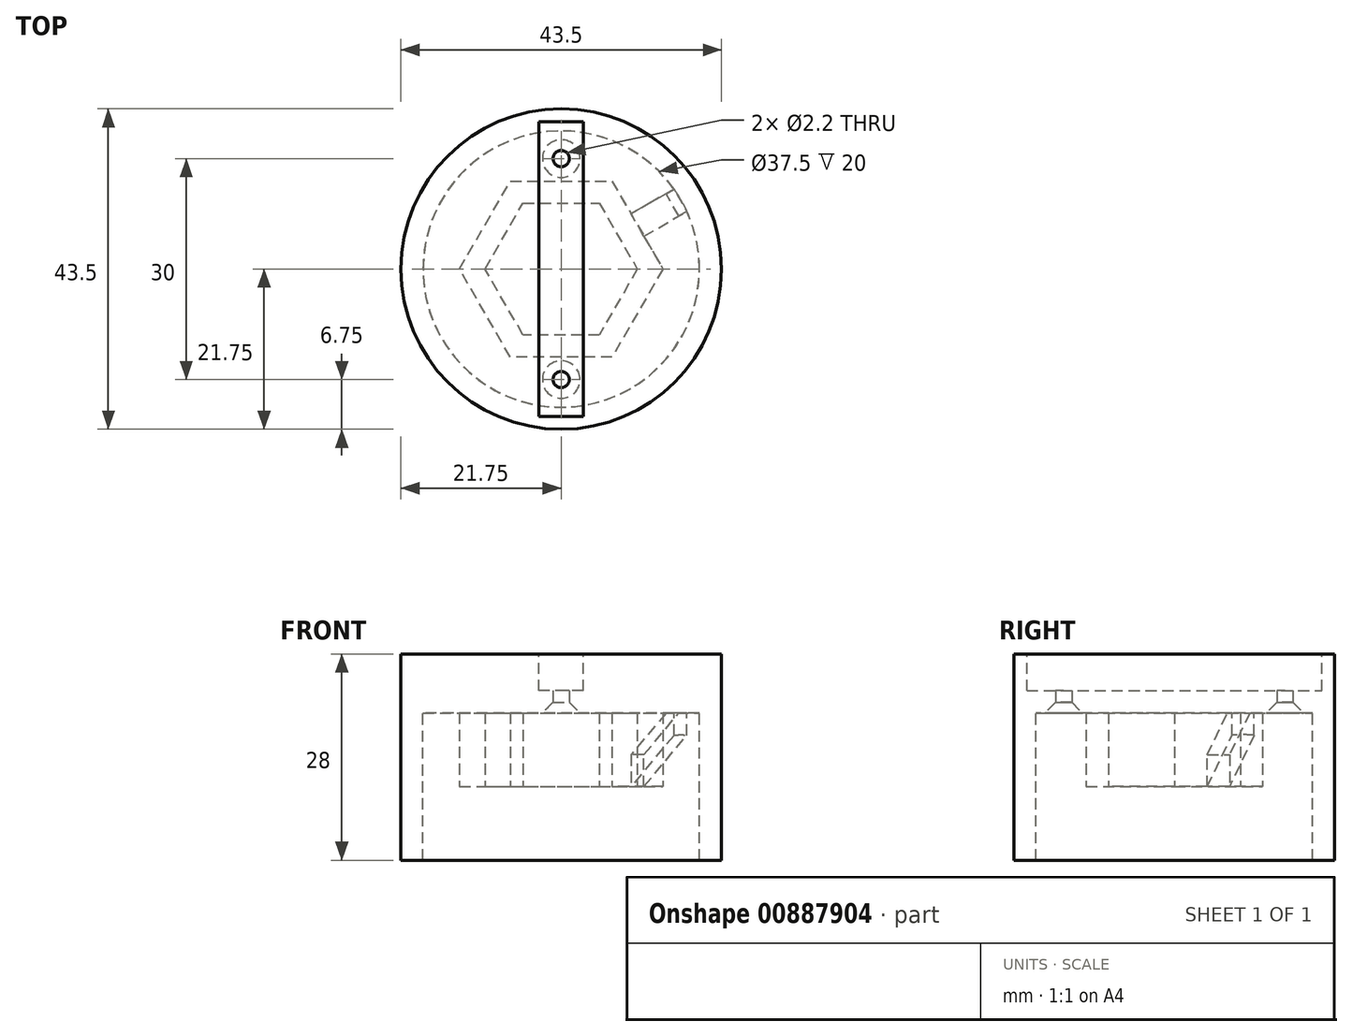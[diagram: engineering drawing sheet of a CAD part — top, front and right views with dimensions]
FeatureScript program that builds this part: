
annotation { "Feature Type Name" : "Feature", "Feature Type Description" : "" }
export const myFeature = defineFeature(function(context is Context, id is Id, definition is map)
    precondition{}
    {
        {
            var Q0;
            Q0=qCreatedBy(makeId("Top.planeOp"),FACE);
            var sketch = newSketch(context, id + "F0", { "sketchPlane" : qUnion([Q0])});
            skCircle(sketch, "E0.cCircle", {"center": v(0, 0) * mm, "radius": 8.95 * mm, "construction": true});
            skLineSegment(sketch, "E0.0", {"start": v(-5.17, 8.95) * mm, "end": v(5.17, 8.95) * mm});
            skLineSegment(sketch, "E0.1", {"start": v(5.17, 8.95) * mm, "end": v(10.33, 0) * mm});
            skLineSegment(sketch, "E0.2", {"start": v(10.33, 0) * mm, "end": v(5.17, -8.95) * mm});
            skLineSegment(sketch, "E0.3", {"start": v(5.17, -8.95) * mm, "end": v(-5.17, -8.95) * mm});
            skLineSegment(sketch, "E0.4", {"start": v(-5.17, -8.95) * mm, "end": v(-10.33, 0) * mm});
            skLineSegment(sketch, "E0.5", {"start": v(-10.33, 0) * mm, "end": v(-5.17, 8.95) * mm});
            skPoint(sketch, "E0.0.midPoint", {"position": v(0, 8.95) * mm});
            skLineSegment(sketch, "E1.0", {"start": v(-6.9, 11.95) * mm, "end": v(6.9, 11.95) * mm});
            skLineSegment(sketch, "E1.1", {"start": v(13.8, 0) * mm, "end": v(6.9, -11.95) * mm});
            skLineSegment(sketch, "E1.2", {"start": v(6.9, -11.95) * mm, "end": v(-6.9, -11.95) * mm});
            skLineSegment(sketch, "E1.3", {"start": v(6.9, 11.95) * mm, "end": v(13.8, 0) * mm});
            skLineSegment(sketch, "E1.4", {"start": v(-6.9, -11.95) * mm, "end": v(-13.8, 0) * mm});
            skLineSegment(sketch, "E1.5", {"start": v(-13.8, 0) * mm, "end": v(-6.9, 11.95) * mm});
            skSolve(sketch);
        }
        {
            var Q0;
            Q0=makeQuery(id+"F0.imprint","IMPRINT",FACE,{"disambiguationData":[TD([[makeQuery(id+"F0.imprint","IMPRINT",EDGE,{"derivedFrom":sQuery(id+"F0.wireOp",EDGE,"E0.0")}),1.0]])]});
            extrude(context, id + "F1", {"entities" : qUnion([Q0]), "depth" : 10 * mm, "offsetDistance" : 25 * mm});
        }
        {
            var Q0;
            Q0=makeQuery(id+"F1.opExtrude","CAP_FACE",FACE,{"disambiguationData":[OSD([sQuery(id+"F0.wireOp",EDGE,"E0.0"),sQuery(id+"F0.wireOp",EDGE,"E0.1"),sQuery(id+"F0.wireOp",EDGE,"E0.2"),sQuery(id+"F0.wireOp",EDGE,"E0.3"),sQuery(id+"F0.wireOp",EDGE,"E0.4"),sQuery(id+"F0.wireOp",EDGE,"E0.5"),sQuery(id+"F0.wireOp",EDGE,"E1.0"),sQuery(id+"F0.wireOp",EDGE,"E1.1"),sQuery(id+"F0.wireOp",EDGE,"E1.2"),sQuery(id+"F0.wireOp",EDGE,"E1.3"),sQuery(id+"F0.wireOp",EDGE,"E1.4"),sQuery(id+"F0.wireOp",EDGE,"E1.5")])],"isStart":false});
            var sketch = newSketch(context, id + "F2", { "sketchPlane" : qUnion([Q0])});
            skCircle(sketch, "E2", {"center": v(0, 0) * mm, "radius": 21.75 * mm});
            skCircle(sketch, "E3.0", {"center": v(0, 0) * mm, "radius": 18.75 * mm});
            skSolve(sketch);
        }
        {
            var Q0;
            Q0=makeQuery(id+"F2.imprint","IMPRINT",FACE,{"disambiguationData":[TD([[makeQuery(id+"F2.imprint","IMPRINT",EDGE,{"derivedFrom":sQuery(id+"F2.wireOp",EDGE,"E2")}),1.0]])]});
            extrude(context, id + "F3", {"entities" : qUnion([Q0]), "oppositeDirection" : true, "depth" : 20 * mm, "offsetDistance" : 25 * mm});
        }
        {
            var Q0;
            Q0=makeQuery(id+"F2.imprint","IMPRINT",FACE,{"disambiguationData":[TD([[makeQuery(id+"F2.imprint","IMPRINT",EDGE,{"derivedFrom":sQuery(id+"F2.wireOp",EDGE,"E3.0")}),1.0]])]});
            var Q1;
            Q1=makeQuery(id+"F2.imprint","IMPRINT",FACE,{"disambiguationData":[TD([[makeQuery(id+"F2.imprint","IMPRINT",EDGE,{"derivedFrom":sQuery(id+"F2.wireOp",EDGE,"E2")}),1.0]])]});
            var Q2;
            Q2=makeQuery(id+"F2.imprint","IMPRINT",FACE,{"disambiguationData":[TD([[makeQuery(id+"F2.imprint","IMPRINT",EDGE,{"derivedFrom":makeQuery(id+"F1.opExtrude","CAP_EDGE",EDGE,{"disambiguationData":[OSD([sQuery(id+"F0.wireOp",EDGE,"E0.0")])],"isStart":false})}),-1.0]])]});
            var Q3;
            Q3=makeQuery(id+"F2.imprint","IMPRINT",FACE,{"disambiguationData":[TD([[makeQuery(id+"F2.imprint","IMPRINT",EDGE,{"derivedFrom":makeQuery(id+"F1.opExtrude","CAP_EDGE",EDGE,{"disambiguationData":[OSD([sQuery(id+"F0.wireOp",EDGE,"E0.0")])],"isStart":false})}),1.0]])]});
            extrude(context, id + "F4", {"entities" : qUnion([Q0, Q1, Q2, Q3]), "depth" : 8 * mm, "offsetDistance" : 25 * mm});
        }
        {
            var Q0;
            Q0=makeQuery(id+"F1.opExtrude","CAP_EDGE",EDGE,{"disambiguationData":[OSD([sQuery(id+"F0.wireOp",EDGE,"E1.3")])],"isStart":true});
            cPlane(context, id + "F5", {"entities" : qUnion([Q0]), "cplaneType" : CPlaneType.LINE_ANGLE, "offset" : 25 * mm, "angle" : 46 * degree, "width" : 150 * mm, "height" : 150 * mm});
        }
        {
            var Q0;
            Q0=qCreatedBy(id+"F5.planeOp",FACE);
            var sketch = newSketch(context, id + "F6", { "sketchPlane" : qUnion([Q0])});
            skLineSegment(sketch, "E4", {"start": v(5.27, -6.65) * mm, "end": v(7.5, -3.96) * mm});
            skLineSegment(sketch, "E5", {"start": v(7.5, -3.96) * mm, "end": v(18.23, -12.88) * mm});
            skLineSegment(sketch, "E6", {"start": v(18.23, -12.88) * mm, "end": v(16, -15.57) * mm});
            skLineSegment(sketch, "E7", {"start": v(16, -15.57) * mm, "end": v(5.27, -6.65) * mm});
            skSolve(sketch);
        }
        {
            var Q0;
            Q0=makeQuery(id+"F6.imprint","IMPRINT",FACE,{"disambiguationData":[TD([[makeQuery(id+"F6.imprint","IMPRINT",EDGE,{"derivedFrom":sQuery(id+"F6.wireOp",EDGE,"E4")}),-1.0]])]});
            var Q1;
            Q1=makeQuery(id+"F4.opExtrude","SWEPT_BODY",BODY,{"disambiguationData":[OSD([sQuery(id+"F2.wireOp",EDGE,"E2")])]});
            extrude(context, id + "F7", {"entities" : qUnion([Q0]), "operationType" : NewBodyOperationType.ADD, "oppositeDirection" : true, "depth" : 3 * mm, "endBoundEntityBody" : qUnion([Q1]), "offsetDistance" : 25 * mm});
        }
        {
            var Q0;
            Q0=makeQuery(id+"F4.opExtrude","CAP_FACE",FACE,{"disambiguationData":[OSD([sQuery(id+"F2.wireOp",EDGE,"E2")])],"isStart":false});
            var sketch = newSketch(context, id + "F8", { "sketchPlane" : qUnion([Q0])});
            skLineSegment(sketch, "E8.bottom", {"start": v(3, -20) * mm, "end": v(-3, -20) * mm});
            skLineSegment(sketch, "E8.top", {"start": v(3, 20) * mm, "end": v(-3, 20) * mm});
            skLineSegment(sketch, "E8.left", {"start": v(3, -20) * mm, "end": v(3, 20) * mm});
            skLineSegment(sketch, "E8.right", {"start": v(-3, -20) * mm, "end": v(-3, 20) * mm});
            skPoint(sketch, "E8.middle", {"position": v(0, 0) * mm});
            skSolve(sketch);
        }
        {
            var Q0;
            Q0=makeQuery(id+"F8.imprint","IMPRINT",FACE,{"disambiguationData":[TD([[makeQuery(id+"F8.imprint","IMPRINT",EDGE,{"derivedFrom":sQuery(id+"F8.wireOp",EDGE,"E8.bottom")}),-1.0]])]});
            extrude(context, id + "F9", {"entities" : qUnion([Q0]), "operationType" : NewBodyOperationType.REMOVE, "oppositeDirection" : true, "depth" : 5 * mm, "offsetDistance" : 25 * mm});
        }
        {
            var Q0;
            Q0=makeQuery(id+"F2.imprint","IMPRINT",FACE,{"disambiguationData":[TD([[makeQuery(id+"F2.imprint","IMPRINT",EDGE,{"derivedFrom":makeQuery(id+"F1.opExtrude","CAP_EDGE",EDGE,{"disambiguationData":[OSD([sQuery(id+"F0.wireOp",EDGE,"E0.0")])],"isStart":false})}),-1.0]])]});
            var sketch = newSketch(context, id + "F10", { "sketchPlane" : qUnion([Q0])});
            skPoint(sketch, "E9", {"position": v(0, 15) * mm});
            skPoint(sketch, "E10.MirrorP", {"position": v(0, -15) * mm});
            skSolve(sketch);
        }
        {
            var Q0;
            Q0=sQuery(id+"F10.wireOp",VERTEX,"E10.MirrorP");
            var Q1;
            Q1=sQuery(id+"F10.wireOp",VERTEX,"E9");
            var Q2;
            Q2=makeQuery(id+"F1.opExtrude","SWEPT_BODY",BODY,{"disambiguationData":[OSD([sQuery(id+"F0.wireOp",EDGE,"E0.0"),sQuery(id+"F0.wireOp",EDGE,"E0.1"),sQuery(id+"F0.wireOp",EDGE,"E0.2"),sQuery(id+"F0.wireOp",EDGE,"E0.3"),sQuery(id+"F0.wireOp",EDGE,"E0.4"),sQuery(id+"F0.wireOp",EDGE,"E0.5"),sQuery(id+"F0.wireOp",EDGE,"E1.0"),sQuery(id+"F0.wireOp",EDGE,"E1.1"),sQuery(id+"F0.wireOp",EDGE,"E1.2"),sQuery(id+"F0.wireOp",EDGE,"E1.3"),sQuery(id+"F0.wireOp",EDGE,"E1.4"),sQuery(id+"F0.wireOp",EDGE,"E1.5")])]});
            hole(context, id + "F11", {"style" : HoleStyle.C_SINK, "endStyle" : HoleEndStyle.THROUGH, "oppositeDirection" : true, "holeDiameter" : 2.2 * mm, "cSinkDiameter" : 5.1 * mm, "cSinkAngle" : 90 * degree, "majorDiameter" : 3 * mm, "isTappedThrough" : true, "tappedDepth" : 12 * mm, "tapClearance" : 3, "startFromSketch" : true, "locations" : qUnion([Q0, Q1]), "scope" : qUnion([Q2])});
        }
    });
